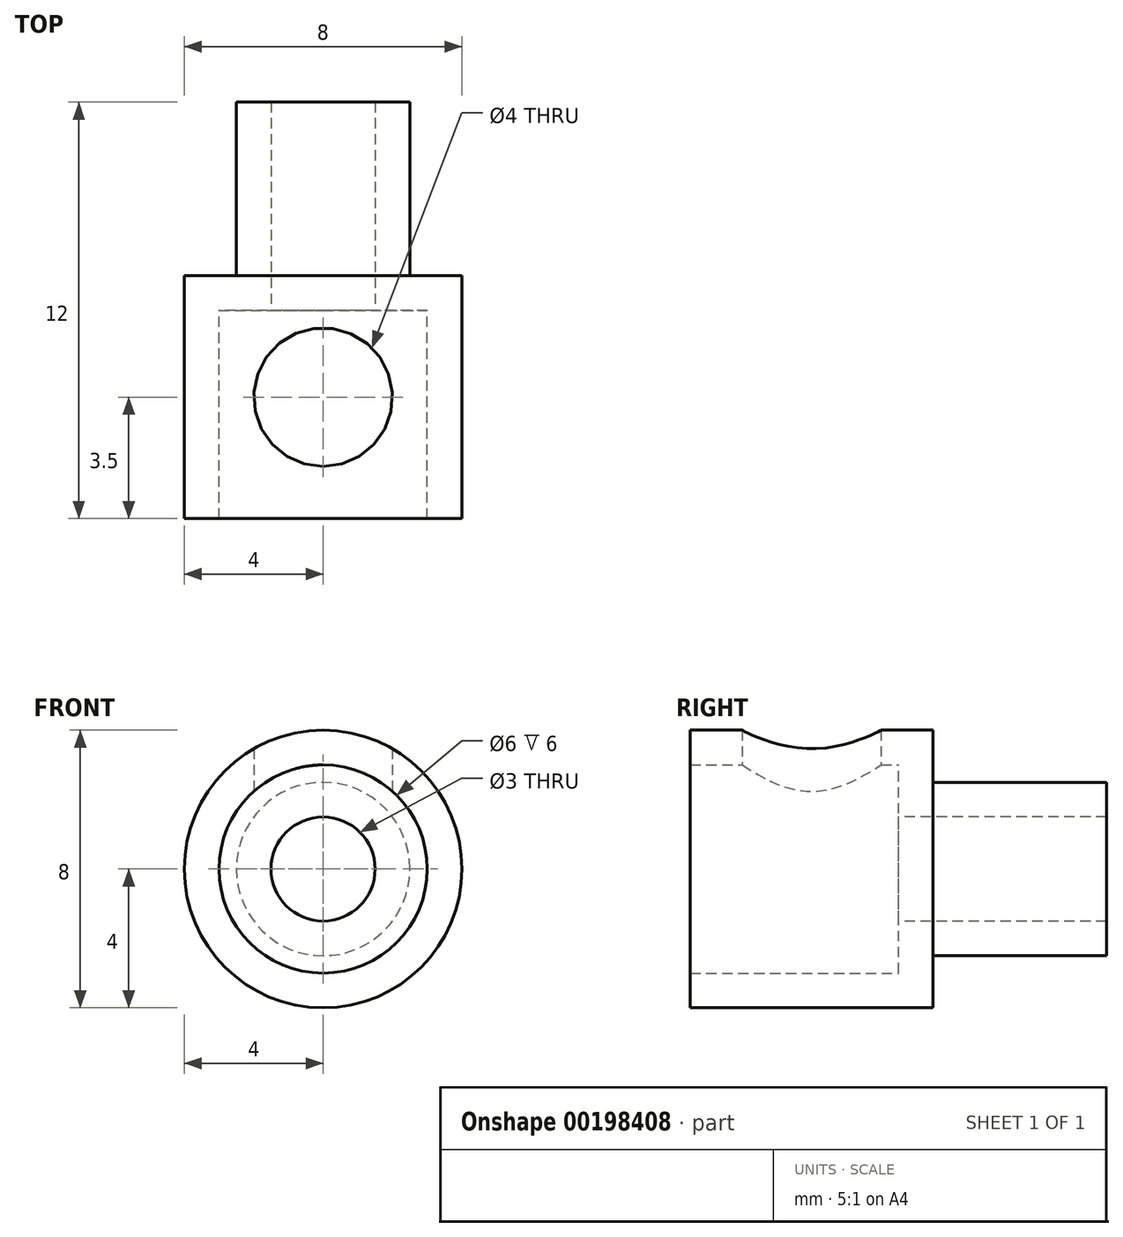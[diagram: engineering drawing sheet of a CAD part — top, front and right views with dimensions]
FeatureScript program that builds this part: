
annotation { "Feature Type Name" : "Feature", "Feature Type Description" : "" }
export const myFeature = defineFeature(function(context is Context, id is Id, definition is map)
    precondition{}
    {
        {
            var Q0;
            Q0=qCreatedBy(makeId("Front.planeOp"),FACE);
            var sketch = newSketch(context, id + "F0", { "sketchPlane" : qUnion([Q0])});
            skCircle(sketch, "E0", {"center": v(0, 0) * mm, "radius": 3 * mm});
            skCircle(sketch, "E1", {"center": v(0, 0) * mm, "radius": 4 * mm});
            skCircle(sketch, "E2", {"center": v(0, 0) * mm, "radius": 2.5 * mm});
            skCircle(sketch, "E3", {"center": v(0, 0) * mm, "radius": 1.5 * mm});
            skSolve(sketch);
        }
        {
            var Q0;
            Q0=makeQuery(id+"F0.imprint","IMPRINT",FACE,{"disambiguationData":[TD([[makeQuery(id+"F0.imprint","IMPRINT",EDGE,{"derivedFrom":sQuery(id+"F0.wireOp",EDGE,"E2")}),1.0]])]});
            extrude(context, id + "F1", {"entities" : qUnion([Q0]), "oppositeDirection" : true, "depth" : 5 * mm});
        }
        {
            var Q0;
            Q0=makeQuery(id+"F0.imprint","IMPRINT",FACE,{"disambiguationData":[TD([[makeQuery(id+"F0.imprint","IMPRINT",EDGE,{"derivedFrom":sQuery(id+"F0.wireOp",EDGE,"E0")}),1.0]])]});
            var Q1;
            Q1=makeQuery(id+"F0.imprint","IMPRINT",FACE,{"disambiguationData":[TD([[makeQuery(id+"F0.imprint","IMPRINT",EDGE,{"derivedFrom":sQuery(id+"F0.wireOp",EDGE,"E0")}),-1.0]])]});
            var Q2;
            Q2=makeQuery(id+"F0.imprint","IMPRINT",FACE,{"disambiguationData":[TD([[makeQuery(id+"F0.imprint","IMPRINT",EDGE,{"derivedFrom":sQuery(id+"F0.wireOp",EDGE,"E2")}),1.0]])]});
            extrude(context, id + "F2", {"entities" : qUnion([Q0, Q1, Q2]), "operationType" : NewBodyOperationType.ADD, "depth" : 1 * mm});
        }
        {
            var Q0;
            Q0=makeQuery(id+"F0.imprint","IMPRINT",FACE,{"disambiguationData":[TD([[makeQuery(id+"F0.imprint","IMPRINT",EDGE,{"derivedFrom":sQuery(id+"F0.wireOp",EDGE,"E0")}),-1.0]])]});
            extrude(context, id + "F3", {"entities" : qUnion([Q0]), "operationType" : NewBodyOperationType.ADD, "depth" : 7 * mm});
        }
        {
            var Q0;
            Q0=qCreatedBy(makeId("Top.planeOp"),FACE);
            var sketch = newSketch(context, id + "F4", { "sketchPlane" : qUnion([Q0])});
            skCircle(sketch, "E4", {"center": v(0, -3.5) * mm, "radius": 2 * mm});
            skSolve(sketch);
        }
        {
            var Q0;
            Q0 = qSketchRegion(id + "F4", true);
            extrude(context, id + "F5", {"entities" : qUnion([Q0]), "operationType" : NewBodyOperationType.REMOVE, "depth" : 25 * mm});
        }
    });
